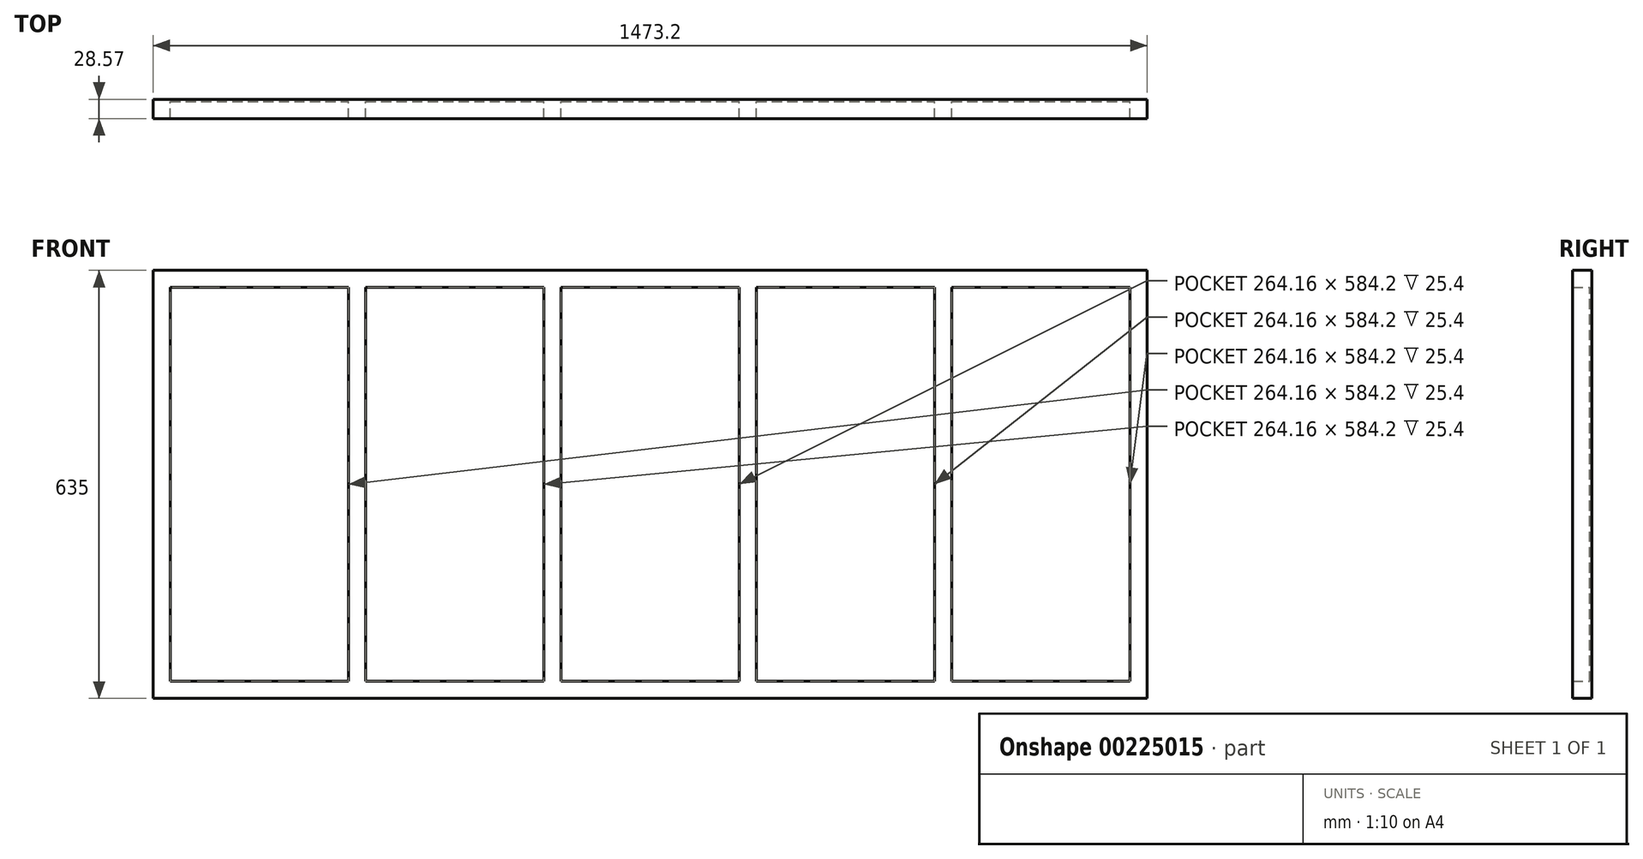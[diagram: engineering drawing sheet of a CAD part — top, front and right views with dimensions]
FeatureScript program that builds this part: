
annotation { "Feature Type Name" : "Feature", "Feature Type Description" : "" }
export const myFeature = defineFeature(function(context is Context, id is Id, definition is map)
    precondition{}
    {
        {
            var Q0;
            Q0=qCreatedBy(makeId("Front.planeOp"),FACE);
            var sketch = newSketch(context, id + "F0", { "sketchPlane" : qUnion([Q0])});
            skLineSegment(sketch, "E0.bottom", {"start": v(0, 0) * mm, "end": v(1473.2, 0) * mm});
            skLineSegment(sketch, "E0.top", {"start": v(0, 635) * mm, "end": v(1473.2, 635) * mm});
            skLineSegment(sketch, "E0.left", {"start": v(0, 0) * mm, "end": v(0, 635) * mm});
            skLineSegment(sketch, "E0.right", {"start": v(1473.2, 0) * mm, "end": v(1473.2, 635) * mm});
            skSolve(sketch);
        }
        {
            var Q0;
            Q0=makeQuery(id+"F0.imprint","IMPRINT",FACE,{"disambiguationData":[TD([[makeQuery(id+"F0.imprint","IMPRINT",EDGE,{"derivedFrom":sQuery(id+"F0.wireOp",EDGE,"E0.bottom")}),1.0]])]});
            extrude(context, id + "F1", {"entities" : qUnion([Q0]), "depth" : 3.17 * mm});
        }
        {
            var Q0;
            Q0=makeQuery(id+"F1.opExtrude","CAP_FACE",FACE,{"disambiguationData":[OSD([sQuery(id+"F0.wireOp",EDGE,"E0.bottom"),sQuery(id+"F0.wireOp",EDGE,"E0.top"),sQuery(id+"F0.wireOp",EDGE,"E0.left"),sQuery(id+"F0.wireOp",EDGE,"E0.right")])],"isStart":false});
            var sketch = newSketch(context, id + "F2", { "sketchPlane" : qUnion([Q0])});
            skLineSegment(sketch, "E1.bottom", {"start": v(0, 0) * mm, "end": v(1473.2, 0) * mm});
            skLineSegment(sketch, "E1.top", {"start": v(0, 25.4) * mm, "end": v(1473.2, 25.4) * mm});
            skLineSegment(sketch, "E1.left", {"start": v(0, 0) * mm, "end": v(0, 25.4) * mm});
            skLineSegment(sketch, "E1.right", {"start": v(1473.2, 0) * mm, "end": v(1473.2, 25.4) * mm});
            skLineSegment(sketch, "E2.bottom", {"start": v(0, 635) * mm, "end": v(1473.2, 635) * mm});
            skLineSegment(sketch, "E2.top", {"start": v(0, 609.6) * mm, "end": v(1473.2, 609.6) * mm});
            skLineSegment(sketch, "E2.left", {"start": v(0, 635) * mm, "end": v(0, 609.6) * mm});
            skLineSegment(sketch, "E2.right", {"start": v(1473.2, 635) * mm, "end": v(1473.2, 609.6) * mm});
            skLineSegment(sketch, "E3.bottom", {"start": v(0, 25.4) * mm, "end": v(25.4, 25.4) * mm});
            skLineSegment(sketch, "E3.top", {"start": v(0, 609.6) * mm, "end": v(25.4, 609.6) * mm});
            skLineSegment(sketch, "E3.left", {"start": v(0, 25.4) * mm, "end": v(0, 609.6) * mm});
            skLineSegment(sketch, "E3.right", {"start": v(25.4, 25.4) * mm, "end": v(25.4, 609.6) * mm});
            skLineSegment(sketch, "E4.1.0.0", {"start": v(314.96, 25.4) * mm, "end": v(314.96, 609.6) * mm});
            skLineSegment(sketch, "E4.1.0.1", {"start": v(289.56, 25.4) * mm, "end": v(289.56, 609.6) * mm});
            skLineSegment(sketch, "E4.2.0.0", {"start": v(604.52, 25.4) * mm, "end": v(604.52, 609.6) * mm});
            skLineSegment(sketch, "E4.2.0.1", {"start": v(579.12, 25.4) * mm, "end": v(579.12, 609.6) * mm});
            skLineSegment(sketch, "E4.3.0.0", {"start": v(894.08, 25.4) * mm, "end": v(894.08, 609.6) * mm});
            skLineSegment(sketch, "E4.3.0.1", {"start": v(868.68, 25.4) * mm, "end": v(868.68, 609.6) * mm});
            skLineSegment(sketch, "E4.4.0.0", {"start": v(1183.64, 25.4) * mm, "end": v(1183.64, 609.6) * mm});
            skLineSegment(sketch, "E4.4.0.1", {"start": v(1158.24, 25.4) * mm, "end": v(1158.24, 609.6) * mm});
            skLineSegment(sketch, "E4.5.0.0", {"start": v(1473.2, 25.4) * mm, "end": v(1473.2, 609.6) * mm});
            skLineSegment(sketch, "E4.5.0.1", {"start": v(1447.8, 25.4) * mm, "end": v(1447.8, 609.6) * mm});
            skLineSegment(sketch, "E4.direction1", {"start": v(25.4, 25.4) * mm, "end": v(314.96, 25.4) * mm, "construction": true});
            skSolve(sketch);
        }
        {
            var Q0;
            Q0=qSketchRegion(id+"F2",true);
            var Q1;
            {var subQ0=sQuery(id+"F2.wireOp",EDGE,"E4.1.0.0");Q1=makeQuery(id+"F2.imprint","IMPRINT",FACE,{"disambiguationData":[TD([[makeQuery(id+"F2.imprint","IMPRINT",EDGE,{"derivedFrom":subQ0}),1.0]])]});}
            var Q2;
            {var subQ0=sQuery(id+"F2.wireOp",EDGE,"E4.2.0.0");Q2=makeQuery(id+"F2.imprint","IMPRINT",FACE,{"disambiguationData":[TD([[makeQuery(id+"F2.imprint","IMPRINT",EDGE,{"derivedFrom":subQ0}),1.0]])]});}
            var Q3;
            {var subQ0=sQuery(id+"F2.wireOp",EDGE,"E4.3.0.0");Q3=makeQuery(id+"F2.imprint","IMPRINT",FACE,{"disambiguationData":[TD([[makeQuery(id+"F2.imprint","IMPRINT",EDGE,{"derivedFrom":subQ0}),1.0]])]});}
            var Q4;
            {var subQ0=sQuery(id+"F2.wireOp",EDGE,"E4.4.0.0");Q4=makeQuery(id+"F2.imprint","IMPRINT",FACE,{"disambiguationData":[TD([[makeQuery(id+"F2.imprint","IMPRINT",EDGE,{"derivedFrom":subQ0}),1.0]])]});}
            extrude(context, id + "F3", {"entities" : qUnion([Q0, Q1, Q2, Q3, Q4]), "operationType" : NewBodyOperationType.ADD, "depth" : 25.4 * mm});
        }
    });
